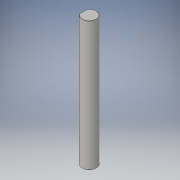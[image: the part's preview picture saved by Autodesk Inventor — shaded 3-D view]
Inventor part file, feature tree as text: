
AUTODESK INVENTOR PART (.ipt)
format: ipt  version: 2016 (Build 200138000, 138)  size: 101,888 bytes
history: native  units: in
note: dims shown in document units (in); Inventor stores cm internally (conversion verified against a paired STEP export)
features: chamfer x1
ambient origin geometry x8: Origin, YZ Plane, XZ Plane, XY Plane, X Axis, Y Axis, Z Axis, Center Point
bodies: Solid1 (feature_tree)
feature tree (1):
  chamfer  "Chamfer1"  [1 undecoded]
note: 1 required parameter value undecoded (feature->parameter linkage not recoverable at this tier; creation-order binding heuristic only, values carry confidence <= 0.55)
